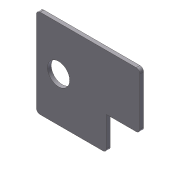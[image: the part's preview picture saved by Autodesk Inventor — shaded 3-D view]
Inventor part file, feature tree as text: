
AUTODESK INVENTOR PART (.ipt)
format: ipt  version: 2012 (Build 160160000, 160)  size: 96,256 bytes
history: native  units: in
note: dims shown in document units (in); Inventor stores cm internally (conversion verified against a paired STEP export)
features: extrude x3, sketch x3, fillet x1
ambient origin geometry x8: Origin, YZ Plane, XZ Plane, XY Plane, X Axis, Y Axis, Z Axis, Center Point
bodies: Solid1 (feature_tree)
feature tree (7):
  extrude  "Extrusion1"  Depth=3.5in
  extrude  "Extrusion3"  Depth=1.125in
  extrude  "Extrusion4"  Depth=0.75in
  fillet  "Fillet1"  Radius=1.5in
  sketch  "Sketch1"  dims[d2=0.125in d3=0.0in d9=3.5in]
  sketch  "Sketch3"  dims[d10=3.0in d12=1.125in]
  sketch  "Sketch4"  dims[d13=0.125in d14=0.0in d15=0.75in d16=1.5in d17=0.75in d18=0.125in d19=0.0in d20=0.125in]
